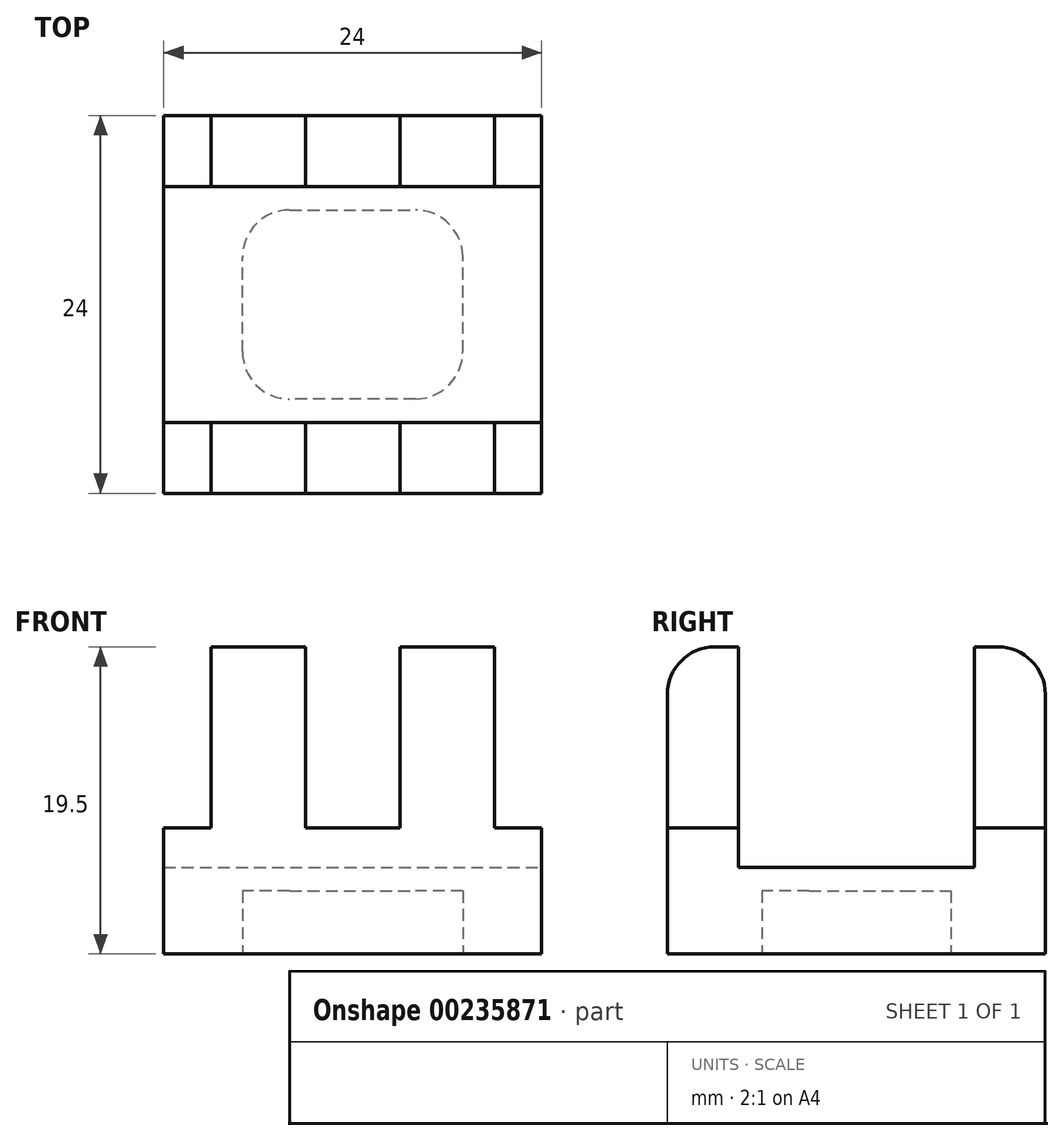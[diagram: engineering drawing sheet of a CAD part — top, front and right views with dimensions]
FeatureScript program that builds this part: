
annotation { "Feature Type Name" : "Feature", "Feature Type Description" : "" }
export const myFeature = defineFeature(function(context is Context, id is Id, definition is map)
    precondition{}
    {
        {
            var Q0;
            Q0=qCreatedBy(makeId("Front.planeOp"),FACE);
            var sketch = newSketch(context, id + "F0", { "sketchPlane" : qUnion([Q0])});
            skLineSegment(sketch, "E0.0", {"start": v(0, -11.5) * mm, "end": v(-3, -11.5) * mm});
            skLineSegment(sketch, "E1", {"start": v(-3, -11.5) * mm, "end": v(-3, 0) * mm});
            skLineSegment(sketch, "E2", {"start": v(-3, 0) * mm, "end": v(-9, 0) * mm});
            skLineSegment(sketch, "E3", {"start": v(-9, 0) * mm, "end": v(-9, -11.5) * mm});
            skLineSegment(sketch, "E4", {"start": v(-7, -19.5) * mm, "end": v(-12, -19.5) * mm});
            skLineSegment(sketch, "E5", {"start": v(-12, -19.5) * mm, "end": v(-12, -11.5) * mm});
            skLineSegment(sketch, "E6", {"start": v(-12, -11.5) * mm, "end": v(-9, -11.5) * mm});
            skLineSegment(sketch, "E7.MirrorCS", {"start": v(0, -11.5) * mm, "end": v(3, -11.5) * mm});
            skLineSegment(sketch, "E8.MirrorCS", {"start": v(3, -11.5) * mm, "end": v(3, 0) * mm});
            skLineSegment(sketch, "E9.MirrorCS", {"start": v(3, 0) * mm, "end": v(9, 0) * mm});
            skLineSegment(sketch, "E10.MirrorCS", {"start": v(9, 0) * mm, "end": v(9, -11.5) * mm});
            skLineSegment(sketch, "E11.MirrorCS", {"start": v(12, -11.5) * mm, "end": v(9, -11.5) * mm});
            skLineSegment(sketch, "E12.MirrorCS", {"start": v(12, -19.5) * mm, "end": v(12, -11.5) * mm});
            skLineSegment(sketch, "E13.MirrorCS", {"start": v(7, -19.5) * mm, "end": v(12, -19.5) * mm});
            skLineSegment(sketch, "E14", {"start": v(-7, -19.5) * mm, "end": v(7, -19.5) * mm});
            skSolve(sketch);
        }
        {
            var Q0;
            Q0 = qSketchRegion(id + "F0", true);
            extrude(context, id + "F1", {"entities" : qUnion([Q0]), "depth" : 24 * mm});
        }
        {
            var Q0;
            Q0=qCreatedBy(makeId("Right.planeOp"),FACE);
            var sketch = newSketch(context, id + "F2", { "sketchPlane" : qUnion([Q0])});
            skLineSegment(sketch, "E15", {"start": v(0, 0) * mm, "end": v(-4.5, 0) * mm});
            skLineSegment(sketch, "E16.trimOffspring", {"start": v(-19.5, 0) * mm, "end": v(-24, 0) * mm});
            skLineSegment(sketch, "E17", {"start": v(-19.5, 0) * mm, "end": v(-19.5, -14) * mm});
            skLineSegment(sketch, "E18", {"start": v(-19.5, -14) * mm, "end": v(-4.5, -14) * mm});
            skLineSegment(sketch, "E19", {"start": v(-4.5, -14) * mm, "end": v(-4.5, 0) * mm});
            skLineSegment(sketch, "E20", {"start": v(-4.5, 0) * mm, "end": v(-19.5, 0) * mm});
            skSolve(sketch);
        }
        {
            var Q0;
            Q0=makeQuery(id+"F1.opExtrude","CAP_EDGE",EDGE,{"disambiguationData":[OSD([sQuery(id+"F0.wireOp",EDGE,"E2")])],"isStart":false});
            var Q1;
            Q1=makeQuery(id+"F1.opExtrude","CAP_EDGE",EDGE,{"disambiguationData":[OSD([sQuery(id+"F0.wireOp",EDGE,"E9.MirrorCS")])],"isStart":false});
            var Q2;
            Q2=makeQuery(id+"F1.opExtrude","CAP_EDGE",EDGE,{"disambiguationData":[OSD([sQuery(id+"F0.wireOp",EDGE,"E9.MirrorCS")])],"isStart":true});
            var Q3;
            Q3=makeQuery(id+"F1.opExtrude","CAP_EDGE",EDGE,{"disambiguationData":[OSD([sQuery(id+"F0.wireOp",EDGE,"E2")])],"isStart":true});
            fillet(context, id + "F3", {"entities" : qUnion([Q0, Q1, Q2, Q3]), "radius" : 3 * mm, "tangentPropagation" : true, "allowEdgeOverflow" : false});
        }
        {
            var Q0;
            Q0=makeQuery(id+"F2.imprint","IMPRINT",FACE,{"disambiguationData":[TD([[makeQuery(id+"F2.imprint","IMPRINT",EDGE,{"derivedFrom":sQuery(id+"F2.wireOp",EDGE,"E17")}),1.0]])]});
            extrude(context, id + "F4", {"entities" : qUnion([Q0]), "operationType" : NewBodyOperationType.REMOVE, "oppositeDirection" : true, "depth" : 25 * mm, "symmetric" : true});
        }
        {
            var Q0;
            Q0=qCreatedBy(makeId("Top.planeOp"),FACE);
            cPlane(context, id + "F5", {"entities" : qUnion([Q0]), "cplaneType" : CPlaneType.OFFSET, "offset" : 19.5 * mm, "oppositeDirection" : true, "width" : 150 * mm, "height" : 150 * mm});
        }
        {
            var Q0;
            Q0=qCreatedBy(id+"F5.planeOp",FACE);
            var sketch = newSketch(context, id + "F6", { "sketchPlane" : qUnion([Q0])});
            skLineSegment(sketch, "E21.0", {"start": v(0, -18) * mm, "end": v(4, -18) * mm});
            skLineSegment(sketch, "E22.0", {"start": v(0, -6) * mm, "end": v(4, -6) * mm});
            skLineSegment(sketch, "E23.MirrorCS", {"start": v(0, -6) * mm, "end": v(-4, -6) * mm});
            skLineSegment(sketch, "E24.MirrorCS", {"start": v(0, -18) * mm, "end": v(-4, -18) * mm});
            skLineSegment(sketch, "E25", {"start": v(7, -15) * mm, "end": v(7, -9) * mm});
            skLineSegment(sketch, "E26", {"start": v(-7, -15) * mm, "end": v(-7, -9) * mm});
            skPoint(sketch, "E27.visualSharp", {"position": v(-7, -6) * mm});
            skArc(sketch, "E27.filletArc", {"start": v(-4, -6) * mm, "mid": v(-6.12, -6.88) * mm, "end": v(-7, -9) * mm});
            skPoint(sketch, "E28.visualSharp", {"position": v(7, -6) * mm});
            skArc(sketch, "E28.filletArc", {"start": v(7, -9) * mm, "mid": v(6.12, -6.88) * mm, "end": v(4, -6) * mm});
            skPoint(sketch, "E29.visualSharp", {"position": v(7, -18) * mm});
            skArc(sketch, "E29.filletArc", {"start": v(4, -18) * mm, "mid": v(6.12, -17.12) * mm, "end": v(7, -15) * mm});
            skPoint(sketch, "E30.visualSharp", {"position": v(-7, -18) * mm});
            skArc(sketch, "E30.filletArc", {"start": v(-7, -15) * mm, "mid": v(-6.12, -17.12) * mm, "end": v(-4, -18) * mm});
            skSolve(sketch);
        }
        {
            var Q0;
            Q0 = qSketchRegion(id + "F6", true);
            extrude(context, id + "F7", {"entities" : qUnion([Q0]), "operationType" : NewBodyOperationType.REMOVE, "depth" : 4 * mm});
        }
    });
